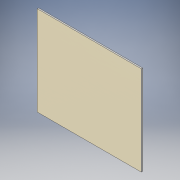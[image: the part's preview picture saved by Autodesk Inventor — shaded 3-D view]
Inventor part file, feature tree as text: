
AUTODESK INVENTOR PART (.ipt)
format: ipt  version: 2019 (Build 230136000, 136)  size: 93,696 bytes
history: native  units: in
note: dims shown in document units (in); Inventor stores cm internally (conversion verified against a paired STEP export)
features: extrude x1, sketch x1
ambient origin geometry x8: Origin, YZ Plane, XZ Plane, XY Plane, X Axis, Y Axis, Z Axis, Center Point
bodies: Solid1 (feature_tree)
feature tree (2):
  extrude  "Extrusion1"  Depth=28.3465in
  sketch  "Sketch1"  dims[d2=0.3937in d3=0.0in d6=28.3465in d7=24.4094in]
